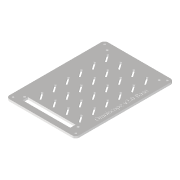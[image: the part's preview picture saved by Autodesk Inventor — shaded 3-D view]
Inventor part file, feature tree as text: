
AUTODESK INVENTOR PART (.ipt)
format: ipt  version: 2022 (Build 260153000, 153)  size: 748,544 bytes
history: native  units: mm
features: extrude x3, sketch x3, reference x2, projected_geometry x2, other x2, pattern_linear x1, hole x1
ambient origin geometry x8: Origin, YZ Plane, XZ Plane, XY Plane, X Axis, Y Axis, Z Axis, Center Point
bodies: Volumenkörper1 (feature_tree)
feature tree (14):
  extrude  "Extrusion1"  Depth=127.5mm
  extrude  "Extrusion5"  Depth=5.0mm
  pattern_linear  "Rechteckige Anordnung3"  Spacing1=9.599311mm  [1 undecoded]
  hole  "Bohrung3"  [1 undecoded]
  extrude  "Extrusion6"  Depth=6.108652mm
  reference  "Referenz1"
  sketch  "Skizze8"  dims[d0=85.5mm d1=127.5mm]
  reference  "Referenz2"
  projected_geometry  "Projizierte Kontur18"
  sketch  "Skizze9"  dims[d2=3.0mm d3=0.0mm d47=5.0mm]
  projected_geometry  "Projizierte Kontur19"
  sketch  "Skizze10"  dims[d48=5.0mm d49=9.599311mm d50=2.5mm d51=6.108652mm d55=3.8mm d57=15.0mm d58=4.8mm d59=0.0mm d60=0.0mm d61=60.0mm d63=19.0mm d64=40.0mm d66=19.0mm d67=2.8mm d68=6.0mm d69=4.0mm d70=2.0mm d71=90.0deg d72=14.0mm d73=20.594885mm d74=1.0mm d75=0.0mm d25=1.0mm d26=1.0mm d27=1.0mm d28=0.15mm d29=0.25mm d30=0.375mm d31=14.3117mm d32=0.75mm d33=20.594885mm d34=0.0625mm d35=0.75mm d36=0.375mm]
  other  "Baugruppe1"
  other  "omniscope1:1"
note: 2 required parameter values undecoded (feature->parameter linkage not recoverable at this tier; creation-order binding heuristic only, values carry confidence <= 0.55)
